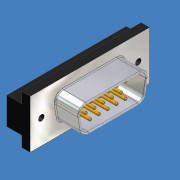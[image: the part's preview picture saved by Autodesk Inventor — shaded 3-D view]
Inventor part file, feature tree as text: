
AUTODESK INVENTOR PART (.ipt)
format: ipt  version: unknown  size: 301,568 bytes
history: native  units: mm (DEFAULTED — no unit token found)
features: sketch x4, extrude x3, fillet x2, hole x1, pattern_linear x1
ambient origin geometry x8: Origin, YZ Plane, XZ Plane, XY Plane, X Axis, Y Axis, Z Axis, Center Point
feature tree (11):
  extrude  "Extrusion1"  Depth=2.16mm
  extrude  "Extrusion2"  Depth=12.5mm
  fillet  "Fillet1"  Radius=30.8mm
  hole  "Hole1"  [1 undecoded]
  extrude  "Extrusion3"  Depth=16.92mm
  fillet  "Fillet2"  Radius=0.5mm
  pattern_linear  "Rectangular Pattern1"  Spacing1=6.1mm  [1 undecoded]
  sketch  "Sketch1"  dims[d2=7.0mm d3=2.16mm]
  sketch  "Sketch2"  dims[d4=6.0mm d5=12.5mm d6=30.8mm d7=0.0mm]
  sketch  "Sketch3"  dims[d8=6.3mm d9=17.453293mm]
  sketch  "Sketch4"  dims[d11=1.5mm d12=16.92mm d13=0.5mm d14=6.1mm d15=0.0mm d16=0.25mm d17=25.0mm d18=1.5mm d19=6.0mm d20=4.0mm d21=2.0mm d22=14.3117mm d23=8.0mm d24=20.594885mm d27=1.98mm d28=4.56mm d29=5.0mm d30=0.0mm d31=0.76mm d32=0.38mm d33=100.0mm d35=1.14mm d36=30.0mm d38=1.98mm]
note: 2 required parameter values undecoded (feature->parameter linkage not recoverable at this tier; creation-order binding heuristic only, values carry confidence <= 0.55)
